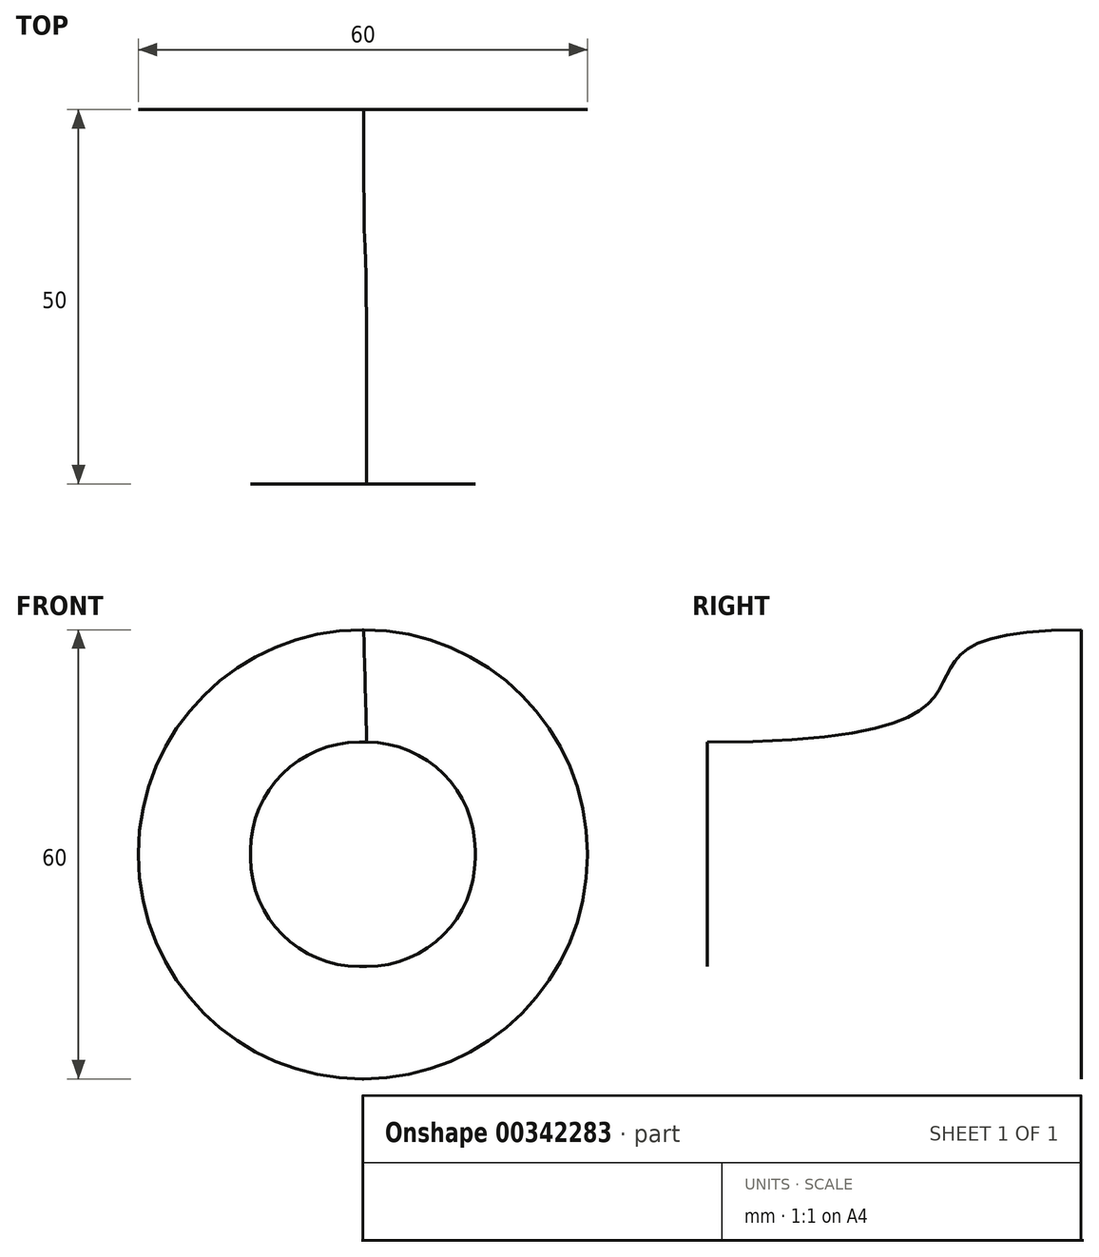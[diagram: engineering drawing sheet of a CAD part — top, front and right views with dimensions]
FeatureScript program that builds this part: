
annotation { "Feature Type Name" : "Feature", "Feature Type Description" : "" }
export const myFeature = defineFeature(function(context is Context, id is Id, definition is map)
    precondition{}
    {
        {
            var Q0;
            Q0=qCreatedBy(makeId("Front.planeOp"),FACE);
            var sketch = newSketch(context, id + "F0", { "sketchPlane" : qUnion([Q0])});
            skLineSegment(sketch, "E0.bottom", {"start": v(0.5, 15) * mm, "end": v(-0.5, 15) * mm});
            skLineSegment(sketch, "E0.top", {"start": v(0.5, -15) * mm, "end": v(-0.5, -15) * mm});
            skLineSegment(sketch, "E0.left", {"start": v(15, 0.5) * mm, "end": v(15, -0.5) * mm});
            skLineSegment(sketch, "E0.right", {"start": v(-15, 0.5) * mm, "end": v(-15, -0.5) * mm});
            skPoint(sketch, "E0.middle", {"position": v(0, 0) * mm});
            skPoint(sketch, "E1.visualSharp", {"position": v(15, 15) * mm});
            skArc(sketch, "E1.filletArc", {"start": v(15, 0.5) * mm, "mid": v(10.75, 10.75) * mm, "end": v(0.5, 15) * mm});
            skPoint(sketch, "E2.visualSharp", {"position": v(15, -15) * mm});
            skArc(sketch, "E2.filletArc", {"start": v(0.5, -15) * mm, "mid": v(10.75, -10.75) * mm, "end": v(15, -0.5) * mm});
            skPoint(sketch, "E3.visualSharp", {"position": v(-15, -15) * mm});
            skArc(sketch, "E3.filletArc", {"start": v(-15, -0.5) * mm, "mid": v(-10.75, -10.75) * mm, "end": v(-0.5, -15) * mm});
            skPoint(sketch, "E4.visualSharp", {"position": v(-15, 15) * mm});
            skArc(sketch, "E4.filletArc", {"start": v(-0.5, 15) * mm, "mid": v(-10.75, 10.75) * mm, "end": v(-15, 0.5) * mm});
            skSolve(sketch);
        }
        {
            var Q0;
            Q0=makeQuery(id+"F0.imprint","IMPRINT",FACE,{"disambiguationData":[TD([[makeQuery(id+"F0.imprint","IMPRINT",EDGE,{"derivedFrom":sQuery(id+"F0.wireOp",EDGE,"E0.bottom")}),1.0]])]});
            extrude(context, id + "F1", {"entities" : qUnion([Q0]), "depth" : 25 * mm});
        }
        {
            var Q0;
            Q0=makeQuery(id+"F1.opExtrude","CAP_FACE",FACE,{"disambiguationData":[OSD([sQuery(id+"F0.wireOp",EDGE,"E0.bottom"),sQuery(id+"F0.wireOp",EDGE,"E0.top"),sQuery(id+"F0.wireOp",EDGE,"E0.left"),sQuery(id+"F0.wireOp",EDGE,"E0.right")])],"isStart":false});
            cPlane(context, id + "F2", {"entities" : qUnion([Q0]), "cplaneType" : CPlaneType.OFFSET, "offset" : 100 * mm, "oppositeDirection" : true, "width" : 150 * mm, "height" : 150 * mm});
        }
        {
            var Q0;
            Q0=qCreatedBy(id+"F2.planeOp",FACE);
            var sketch = newSketch(context, id + "F3", { "sketchPlane" : qUnion([Q0])});
            skLineSegment(sketch, "E5.bottom", {"start": v(0.1, 30) * mm, "end": v(-0.1, 30) * mm});
            skLineSegment(sketch, "E5.top", {"start": v(0.1, -30) * mm, "end": v(-0.1, -30) * mm});
            skLineSegment(sketch, "E5.left", {"start": v(30, 0.1) * mm, "end": v(30, -0.1) * mm});
            skLineSegment(sketch, "E5.right", {"start": v(-30, 0.1) * mm, "end": v(-30, -0.1) * mm});
            skPoint(sketch, "E5.middle", {"position": v(0, 0) * mm});
            skPoint(sketch, "E6.visualSharp", {"position": v(30, 30) * mm});
            skArc(sketch, "E6.filletArc", {"start": v(30, 0.1) * mm, "mid": v(21.24, 21.24) * mm, "end": v(0.1, 30) * mm});
            skPoint(sketch, "E7.visualSharp", {"position": v(30, -30) * mm});
            skArc(sketch, "E7.filletArc", {"start": v(0.1, -30) * mm, "mid": v(21.24, -21.24) * mm, "end": v(30, -0.1) * mm});
            skPoint(sketch, "E8.visualSharp", {"position": v(-30, -30) * mm});
            skArc(sketch, "E8.filletArc", {"start": v(-30, -0.1) * mm, "mid": v(-21.24, -21.24) * mm, "end": v(-0.1, -30) * mm});
            skPoint(sketch, "E9.visualSharp", {"position": v(-30, 30) * mm});
            skArc(sketch, "E9.filletArc", {"start": v(-0.1, 30) * mm, "mid": v(-21.24, 21.24) * mm, "end": v(-30, 0.1) * mm});
            skSolve(sketch);
        }
        {
            var Q0;
            Q0 = qSketchRegion(id + "F3", true);
            extrude(context, id + "F4", {"entities" : qUnion([Q0]), "depth" : 25 * mm});
        }
        {
            var Q0;
            Q0=makeQuery(id+"F1.opExtrude","CAP_FACE",FACE,{"disambiguationData":[OSD([sQuery(id+"F0.wireOp",EDGE,"E0.bottom"),sQuery(id+"F0.wireOp",EDGE,"E0.top"),sQuery(id+"F0.wireOp",EDGE,"E0.left"),sQuery(id+"F0.wireOp",EDGE,"E0.right")])],"isStart":true});
            var Q1;
            Q1=makeQuery(id+"F4.opExtrude","CAP_FACE",FACE,{"disambiguationData":[OSD([sQuery(id+"F3.wireOp",EDGE,"E5.bottom"),sQuery(id+"F3.wireOp",EDGE,"E5.top"),sQuery(id+"F3.wireOp",EDGE,"E5.left"),sQuery(id+"F3.wireOp",EDGE,"E5.right")])],"isStart":false});
            loft(context, id + "F5", {"bodyType" : ToolBodyType.SURFACE, "startCondition" : LoftEndDerivativeType.NORMAL_TO_PROFILE, "startMagnitude" : 3, "endCondition" : LoftEndDerivativeType.MATCH_TANGENT, "endMagnitude" : 2, "wireProfilesArray" : [{ "wireProfileEntities" : qUnion([Q0]) }, { "wireProfileEntities" : qUnion([Q1]) }]});
        }
        {
            var Q0;
            Q0=makeQuery(id+"F4.opExtrude","SWEPT_FACE",FACE,{"disambiguationData":[OSD([sQuery(id+"F3.wireOp",EDGE,"E5.bottom")])]});
            cPlane(context, id + "F6", {"entities" : qUnion([Q0]), "cplaneType" : CPlaneType.OFFSET, "offset" : 30 * mm, "oppositeDirection" : true, "width" : 150 * mm, "height" : 150 * mm});
        }
        {
            var Q0;
            Q0=makeQuery(id+"F1.opExtrude","CAP_FACE",FACE,{"disambiguationData":[OSD([sQuery(id+"F0.wireOp",EDGE,"E0.bottom"),sQuery(id+"F0.wireOp",EDGE,"E0.top"),sQuery(id+"F0.wireOp",EDGE,"E0.left"),sQuery(id+"F0.wireOp",EDGE,"E0.right"),sQuery(id+"F0.wireOp",EDGE,"E1.filletArc"),sQuery(id+"F0.wireOp",EDGE,"E2.filletArc"),sQuery(id+"F0.wireOp",EDGE,"E3.filletArc"),sQuery(id+"F0.wireOp",EDGE,"E4.filletArc")])],"isStart":false});
            extrude(context, id + "F7", {"entities" : qUnion([Q0]), "operationType" : NewBodyOperationType.REMOVE, "oppositeDirection" : true, "depth" : 25 * mm});
        }
        {
            var Q0;
            Q0=makeQuery(id+"F4.opExtrude","CAP_FACE",FACE,{"disambiguationData":[OSD([sQuery(id+"F3.wireOp",EDGE,"E5.bottom"),sQuery(id+"F3.wireOp",EDGE,"E5.top"),sQuery(id+"F3.wireOp",EDGE,"E5.left"),sQuery(id+"F3.wireOp",EDGE,"E5.right"),sQuery(id+"F3.wireOp",EDGE,"E6.filletArc"),sQuery(id+"F3.wireOp",EDGE,"E7.filletArc"),sQuery(id+"F3.wireOp",EDGE,"E8.filletArc"),sQuery(id+"F3.wireOp",EDGE,"E9.filletArc")])],"isStart":true});
            extrude(context, id + "F8", {"entities" : qUnion([Q0]), "operationType" : NewBodyOperationType.REMOVE, "oppositeDirection" : true, "depth" : 25 * mm});
        }
    });
